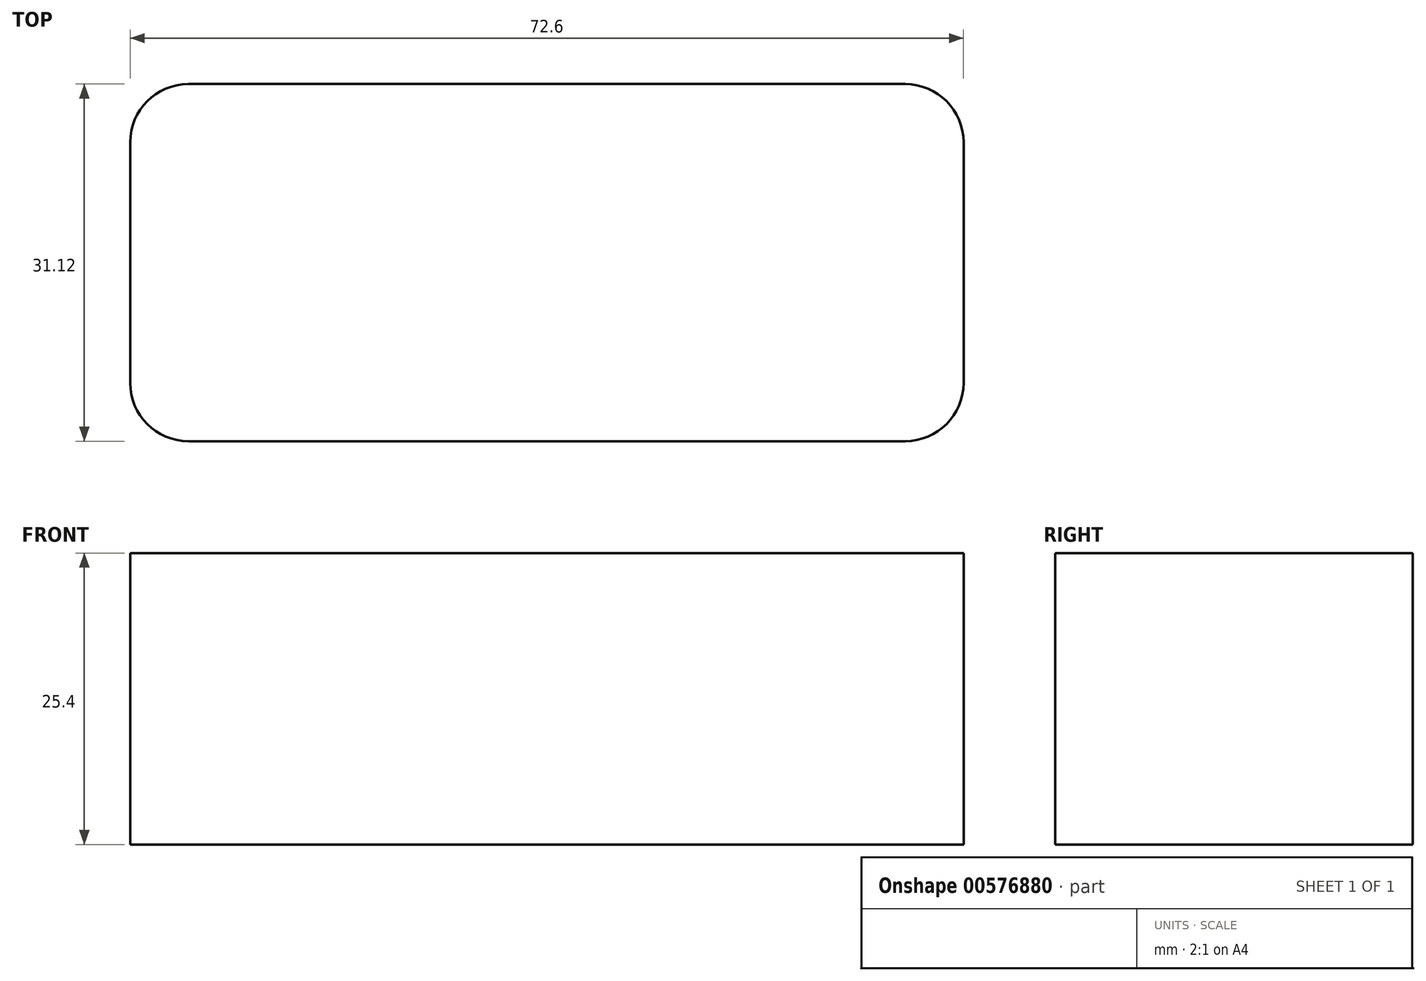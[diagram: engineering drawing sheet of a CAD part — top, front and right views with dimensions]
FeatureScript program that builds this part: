
annotation { "Feature Type Name" : "Feature", "Feature Type Description" : "" }
export const myFeature = defineFeature(function(context is Context, id is Id, definition is map)
    precondition{}
    {
        {
            var Q0;
            Q0=qCreatedBy(makeId("Top.planeOp"),FACE);
            var sketch = newSketch(context, id + "F0", { "sketchPlane" : qUnion([Q0])});
            skPoint(sketch, "E0.0", {"position": v(0, 0) * mm});
            skLineSegment(sketch, "E1.bottom", {"start": v(36.3, -15.56) * mm, "end": v(-36.3, -15.56) * mm});
            skLineSegment(sketch, "E1.top", {"start": v(36.3, 15.56) * mm, "end": v(-36.3, 15.56) * mm});
            skLineSegment(sketch, "E1.left", {"start": v(36.3, -15.56) * mm, "end": v(36.3, 15.56) * mm});
            skLineSegment(sketch, "E1.right", {"start": v(-36.3, -15.56) * mm, "end": v(-36.3, 15.56) * mm});
            skSolve(sketch);
        }
        {
            var Q0;
            Q0=makeQuery(id+"F0.imprint","IMPRINT",FACE,{"disambiguationData":[TD([[makeQuery(id+"F0.imprint","IMPRINT",EDGE,{"derivedFrom":sQuery(id+"F0.wireOp",EDGE,"E1.bottom")}),-1.0]])]});
            extrude(context, id + "F1", {"entities" : qUnion([Q0]), "depth" : 25.4 * mm, "offsetDistance" : 25.4 * mm});
        }
        {
            var Q0;
            Q0=makeQuery(id+"F1.opExtrude","SWEPT_EDGE",EDGE,{"disambiguationData":[OSD([sQuery(id+"F0.wireOp",EDGE,"E1.top"),sQuery(id+"F0.wireOp",EDGE,"E1.left")])]});
            var Q1;
            Q1=makeQuery(id+"F1.opExtrude","SWEPT_EDGE",EDGE,{"disambiguationData":[OSD([sQuery(id+"F0.wireOp",EDGE,"E1.top"),sQuery(id+"F0.wireOp",EDGE,"E1.right")])]});
            var Q2;
            Q2=makeQuery(id+"F1.opExtrude","SWEPT_EDGE",EDGE,{"disambiguationData":[OSD([sQuery(id+"F0.wireOp",EDGE,"E1.bottom"),sQuery(id+"F0.wireOp",EDGE,"E1.left")])]});
            var Q3;
            Q3=makeQuery(id+"F1.opExtrude","SWEPT_EDGE",EDGE,{"disambiguationData":[OSD([sQuery(id+"F0.wireOp",EDGE,"E1.bottom"),sQuery(id+"F0.wireOp",EDGE,"E1.right")])]});
            fillet(context, id + "F2", {"entities" : qUnion([Q0, Q1, Q2, Q3]), "radius" : 5.08 * mm, "tangentPropagation" : true, "allowEdgeOverflow" : false});
        }
    });
